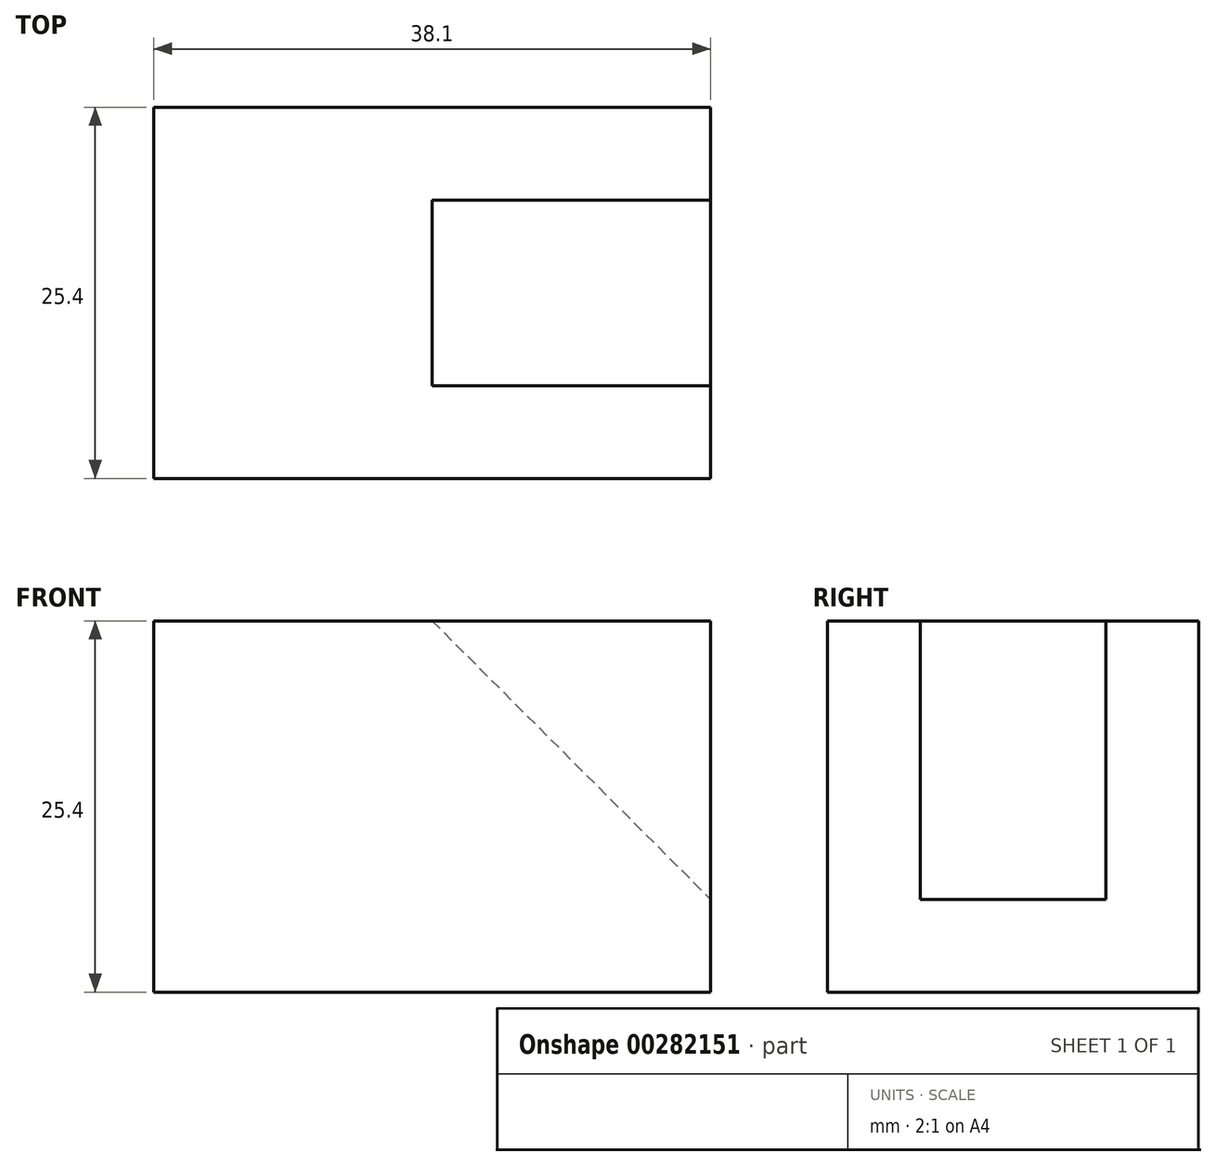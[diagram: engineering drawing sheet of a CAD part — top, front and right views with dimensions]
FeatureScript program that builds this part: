
annotation { "Feature Type Name" : "Feature", "Feature Type Description" : "" }
export const myFeature = defineFeature(function(context is Context, id is Id, definition is map)
    precondition{}
    {
        {
            var Q0;
            Q0=qCreatedBy(makeId("Front.planeOp"),FACE);
            var sketch = newSketch(context, id + "F0", { "sketchPlane" : qUnion([Q0])});
            skLineSegment(sketch, "E0", {"start": v(0, 0) * mm, "end": v(38.1, 0) * mm});
            skLineSegment(sketch, "E1", {"start": v(38.1, 0) * mm, "end": v(38.1, 6.35) * mm});
            skLineSegment(sketch, "E2", {"start": v(0, 0) * mm, "end": v(0, 25.4) * mm});
            skLineSegment(sketch, "E3", {"start": v(0, 25.4) * mm, "end": v(19.05, 25.4) * mm});
            skLineSegment(sketch, "E4", {"start": v(19.05, 25.4) * mm, "end": v(19.05, 6.35) * mm});
            skLineSegment(sketch, "E5", {"start": v(19.05, 6.35) * mm, "end": v(38.1, 6.35) * mm});
            skSolve(sketch);
        }
        {
            var Q0;
            Q0=makeQuery(id+"F0.imprint","IMPRINT",FACE,{"disambiguationData":[TD([[makeQuery(id+"F0.imprint","IMPRINT",EDGE,{"derivedFrom":sQuery(id+"F0.wireOp",EDGE,"E0")}),1.0]])]});
            extrude(context, id + "F1", {"entities" : qUnion([Q0]), "depth" : 25.4 * mm});
        }
        {
            var Q0;
            Q0=makeQuery(id+"F1.opExtrude","CAP_FACE",FACE,{"disambiguationData":[OSD([sQuery(id+"F0.wireOp",EDGE,"E0"),sQuery(id+"F0.wireOp",EDGE,"E1"),sQuery(id+"F0.wireOp",EDGE,"E2"),sQuery(id+"F0.wireOp",EDGE,"E3"),sQuery(id+"F0.wireOp",EDGE,"E4"),sQuery(id+"F0.wireOp",EDGE,"E5")])],"isStart":false});
            var sketch = newSketch(context, id + "F2", { "sketchPlane" : qUnion([Q0])});
            skLineSegment(sketch, "E6", {"start": v(19.05, 25.4) * mm, "end": v(38.1, 6.35) * mm});
            skSolve(sketch);
        }
        {
            var Q0;
            Q0=makeQuery(id+"F2.imprint","IMPRINT",FACE,{"disambiguationData":[TD([[makeQuery(id+"F2.imprint","IMPRINT",EDGE,{"derivedFrom":sQuery(id+"F2.wireOp",EDGE,"E6")}),-1.0]])]});
            extrude(context, id + "F3", {"entities" : qUnion([Q0]), "operationType" : NewBodyOperationType.ADD, "oppositeDirection" : true, "depth" : 25.4 * mm});
        }
        {
            var Q0;
            {var subQ0=sQuery(id+"F0.wireOp",EDGE,"E5");var subQ1=sQuery(id+"F0.wireOp",EDGE,"E4");Q0=makeQuery(id+"F3.boolean.opBoolean","MERGE",FACE,{"derivedFrom":[makeQuery(id+"F1.opExtrude","CAP_FACE",FACE,{"disambiguationData":[OSD([sQuery(id+"F0.wireOp",EDGE,"E0"),sQuery(id+"F0.wireOp",EDGE,"E1"),sQuery(id+"F0.wireOp",EDGE,"E2"),sQuery(id+"F0.wireOp",EDGE,"E3"),subQ1,subQ0])],"isStart":false}),makeQuery(id+"F3.opExtrude","CAP_FACE",FACE,{"disambiguationData":[OSD([subQ1,subQ0,sQuery(id+"F2.wireOp",EDGE,"E6")])],"isStart":true})]});}
            var sketch = newSketch(context, id + "F4", { "sketchPlane" : qUnion([Q0])});
            skLineSegment(sketch, "E7", {"start": v(38.1, 6.35) * mm, "end": v(38.1, 25.4) * mm});
            skLineSegment(sketch, "E8", {"start": v(38.1, 25.4) * mm, "end": v(19.05, 25.4) * mm});
            skSolve(sketch);
        }
        {
            var Q0;
            Q0=makeQuery(id+"F4.imprint","IMPRINT",FACE,{"disambiguationData":[TD([[makeQuery(id+"F4.imprint","IMPRINT",EDGE,{"derivedFrom":sQuery(id+"F4.wireOp",EDGE,"E7")}),1.0]])]});
            extrude(context, id + "F5", {"entities" : qUnion([Q0]), "operationType" : NewBodyOperationType.ADD, "oppositeDirection" : true, "depth" : 6.35 * mm});
        }
        {
            var Q0;
            {var subQ0=sQuery(id+"F0.wireOp",EDGE,"E5");var subQ1=sQuery(id+"F0.wireOp",EDGE,"E4");Q0=makeQuery(id+"F3.boolean.opBoolean","MERGE",FACE,{"derivedFrom":[makeQuery(id+"F1.opExtrude","CAP_FACE",FACE,{"disambiguationData":[OSD([sQuery(id+"F0.wireOp",EDGE,"E0"),sQuery(id+"F0.wireOp",EDGE,"E1"),sQuery(id+"F0.wireOp",EDGE,"E2"),sQuery(id+"F0.wireOp",EDGE,"E3"),subQ1,subQ0])],"isStart":true}),makeQuery(id+"F3.opExtrude","CAP_FACE",FACE,{"disambiguationData":[OSD([subQ1,subQ0,sQuery(id+"F2.wireOp",EDGE,"E6")])],"isStart":false})]});}
            var sketch = newSketch(context, id + "F6", { "sketchPlane" : qUnion([Q0])});
            skLineSegment(sketch, "E9", {"start": v(-19.05, 25.4) * mm, "end": v(-38.1, 25.4) * mm});
            skLineSegment(sketch, "E10", {"start": v(-38.1, 25.4) * mm, "end": v(-38.1, 6.35) * mm});
            skSolve(sketch);
        }
        {
            var Q0;
            Q0 = qSketchRegion(id + "F6", true);
            var Q1;
            Q1=makeQuery(id+"F6.imprint","IMPRINT",FACE,{"disambiguationData":[TD([[makeQuery(id+"F6.imprint","IMPRINT",EDGE,{"derivedFrom":sQuery(id+"F6.wireOp",EDGE,"E9")}),1.0]])]});
            extrude(context, id + "F7", {"entities" : qUnion([Q0, Q1]), "operationType" : NewBodyOperationType.ADD, "oppositeDirection" : true, "depth" : 6.35 * mm});
        }
    });
